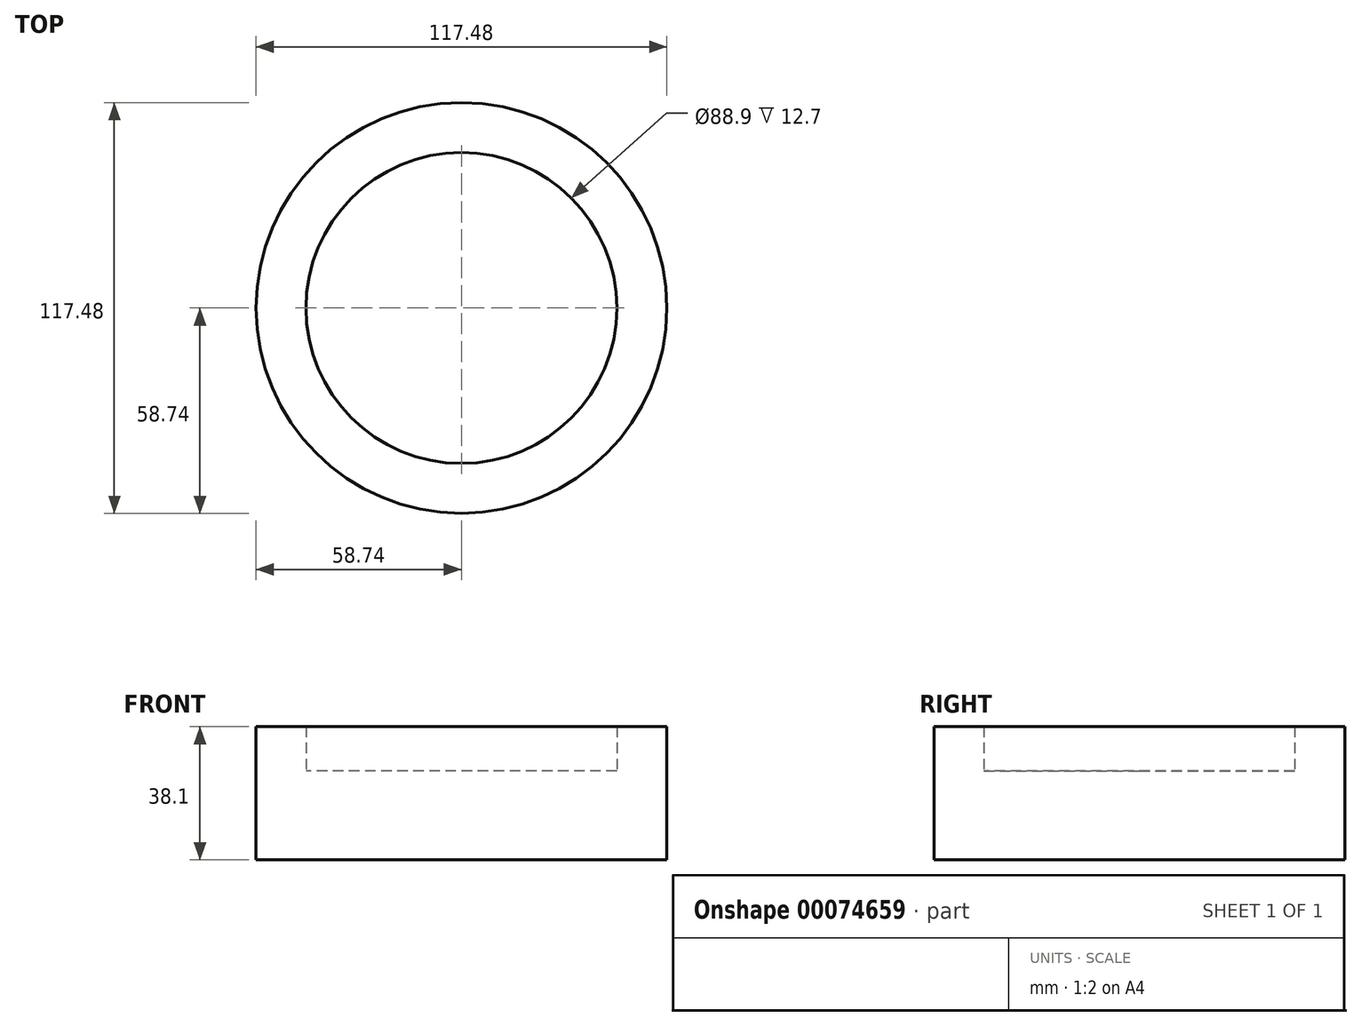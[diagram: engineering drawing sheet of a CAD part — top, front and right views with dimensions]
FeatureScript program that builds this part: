
annotation { "Feature Type Name" : "Feature", "Feature Type Description" : "" }
export const myFeature = defineFeature(function(context is Context, id is Id, definition is map)
    precondition{}
    {
        {
            var Q0;
            Q0=qCreatedBy(makeId("Top.planeOp"),FACE);
            var sketch = newSketch(context, id + "F0", { "sketchPlane" : qUnion([Q0])});
            skCircle(sketch, "E0", {"center": v(0, 0) * mm, "radius": 58.74 * mm});
            skCircle(sketch, "E1", {"center": v(0, 0) * mm, "radius": 44.45 * mm});
            skSolve(sketch);
        }
        {
            var Q0;
            Q0 = qSketchRegion(id + "F0", true);
            extrude(context, id + "F1", {"entities" : qUnion([Q0]), "depth" : 38.1 * mm});
        }
        {
            var Q0;
            Q0=qCreatedBy(makeId("Top.planeOp"),FACE);
            var sketch = newSketch(context, id + "F2", { "sketchPlane" : qUnion([Q0])});
            skCircle(sketch, "E2", {"center": v(0, 0) * mm, "radius": 50.8 * mm});
            skSolve(sketch);
        }
        {
            var Q0;
            Q0 = qSketchRegion(id + "F2", true);
            extrude(context, id + "F3", {"entities" : qUnion([Q0]), "operationType" : NewBodyOperationType.ADD, "depth" : 25.4 * mm});
        }
    });
